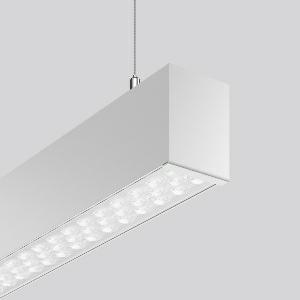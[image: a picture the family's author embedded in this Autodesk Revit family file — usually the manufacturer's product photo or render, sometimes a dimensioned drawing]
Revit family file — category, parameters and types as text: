
# Revit family: linedo_single_ip20_312564_000_1_76_84db
name_source: partatom
category: Lighting Fixtures
units: mm (PartAtom-declared; Revit-internal decimal feet)

## family parameters
Cut with Voids When Loaded = No
Host = Face
Light Source = No
Part Type = Normal
Room Calculation Point = No
Round Connector Dimension = Use Diameter
Shared = No

## types (1)
- LINEDO single IP20 (1 x LED Modul 840, 6450 lm, 4000)
    Apparent Load = 40 VA
    CIE Flux Codes = 86 96 99 100 100
    Color Rendering = 80
    Color Temperature = 4000
    Default Elevation = 1800 mm
    Description = Series: LINEDO single IP20
Stylish pendant luminaire. Housing: extruded aluminium profile, anodised. End cap aluminium powder-coated, without visible screws. High-efficiency LED units with optimum light control thanks to clear plastic (PC) lens optics. 2-point steel cable suspension freely positionable and infinitely height-adjustable. With power cord (2.5 m). Please order canopy separately if required. Perfect for office areas (RUG < 19) and environments with computer screens in accordance with EN 12464-1. 
Colour: anodised aluminium
Length: 2264 mm
Width: 58 mm
Height: 76 mm
Suspension length: 100-1500 mm
Lamp: LED
Socket: without socket
Colour temperature: 4000K
Colour rendering index (CRI): 80
System power: 40 W
Rated luminous flux: 6450 lm
Beam angle Down: 59°
Luminous efficiency: 161 lm/W
Control gear: Converter, dimmable, DALI
Protection class: I
Type of protection: IP 20
    Height = 76 mm
    Lamp = 1 x LED Modul 840
    Lamp Light Flux = 6450 lm
    Lamp count = 1
    Length = 2264 mm
    Lifetime = 50000 h
    Luminous efficacy = 161 lm/W
    Manufacturer = RZB
    ModVariant = No
    Model = 312564.000.1.76
    Mounting Place = Ceiling
    Mounting Type = Pendant
    Number of Poles = 1
    OnlyDefault = Yes
    Power Factor = 1
    Product Name = LINEDO single IP20
    Product group = Pendant luminaires
    ProductGroupID = 902
    Protection Class = Protection class I
    Protection Degree = Degree of protection
    RLX_Detail_Level = 1
    RLX_Emergency_Light_Flux = 0 lm
    RLX_Emergency_Type = 0
    RLX_Emergency_Type_DB = No
    RlxData = <blob elided: 29377 chars, md5=83b3b1fd>
    Socket = socket
    Standby Power = 0 W
    System Light Flux = 6450 lm
    System Power = 40 W
    Type Comments = ALEA SPOT
    Type Image = 312563.000.jpg
    URL = http://relux.com
    VarID = ---
    Voltage = 0 V
    Weight = 0.00 kg
    Width = 58 mm

## geometry (parser evidence)
native form markers: Blend x4, Sweep x11
no freeform markers — native parametric forms only
